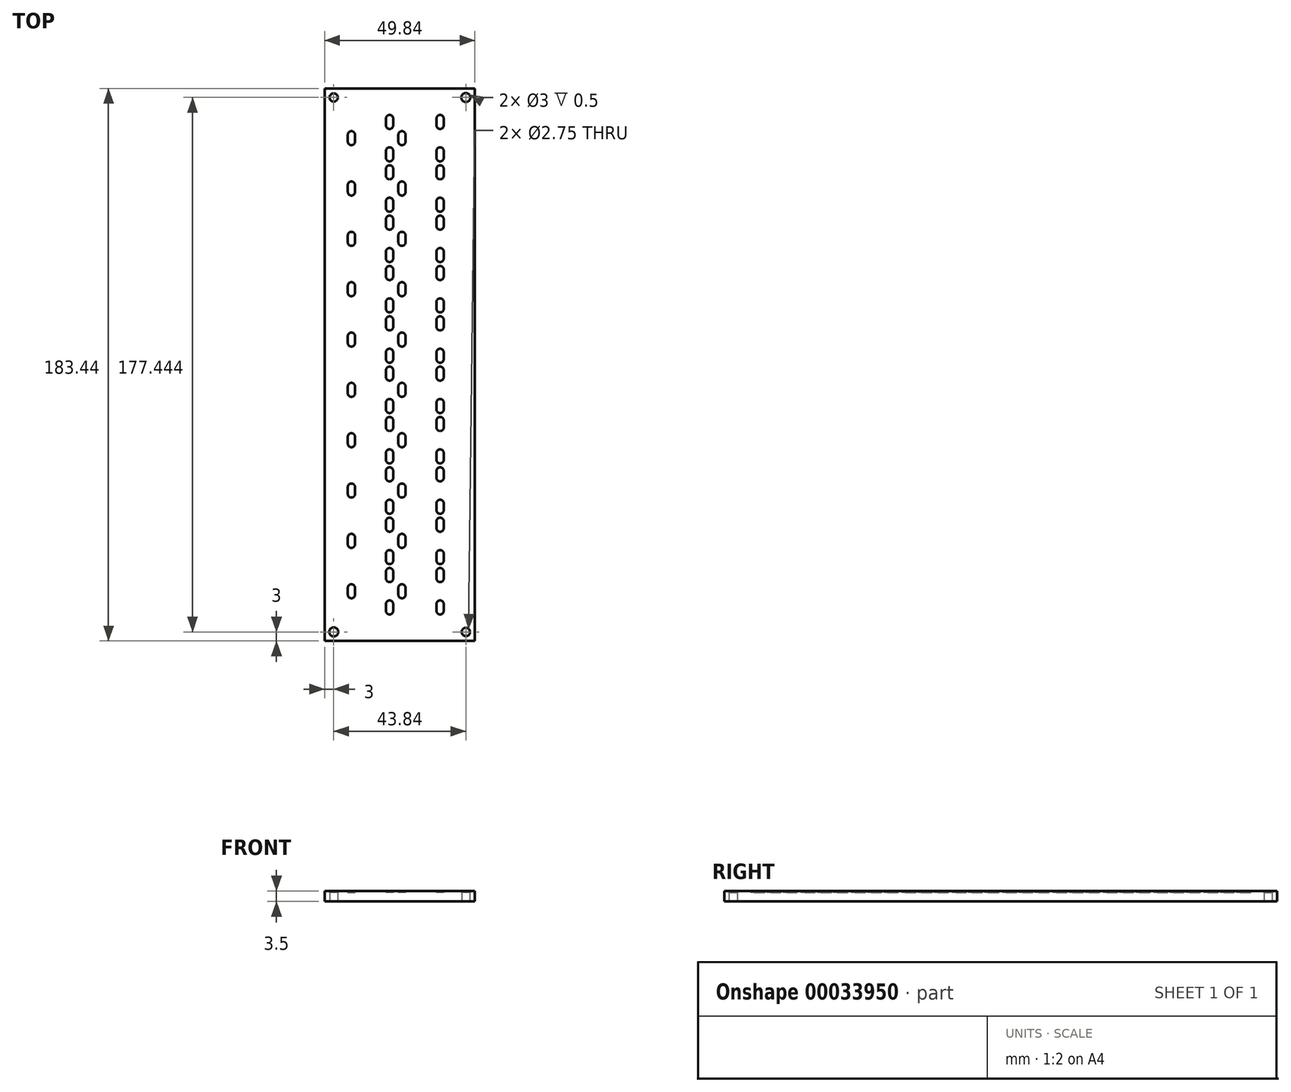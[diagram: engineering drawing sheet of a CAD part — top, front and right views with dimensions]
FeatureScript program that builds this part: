
annotation { "Feature Type Name" : "Feature", "Feature Type Description" : "" }
export const myFeature = defineFeature(function(context is Context, id is Id, definition is map)
    precondition{}
    {
        {
            var Q0;
            Q0=qCreatedBy(makeId("Top.planeOp"),FACE);
            var sketch = newSketch(context, id + "F0", { "sketchPlane" : qUnion([Q0])});
            skCircle(sketch, "E0", {"center": v(0, 0) * mm, "radius": 1.5 * mm});
            skCircle(sketch, "E1", {"center": v(43.84, 177.44) * mm, "radius": 1.5 * mm});
            skLineSegment(sketch, "E2.bottom", {"start": v(-3, 180.44) * mm, "end": v(46.84, 180.44) * mm});
            skLineSegment(sketch, "E2.top", {"start": v(-3, -3) * mm, "end": v(46.84, -3) * mm});
            skLineSegment(sketch, "E2.left", {"start": v(-3, 180.44) * mm, "end": v(-3, -3) * mm});
            skLineSegment(sketch, "E2.right", {"start": v(46.84, 180.44) * mm, "end": v(46.84, -3) * mm});
            skLineSegment(sketch, "E3.rect.left", {"start": v(19.73, 6.99) * mm, "end": v(19.73, 9.29) * mm});
            skLineSegment(sketch, "E3.rect.right", {"start": v(17.35, 6.99) * mm, "end": v(17.35, 9.29) * mm});
            skPoint(sketch, "E3.rect.middle", {"position": v(18.54, 8.14) * mm});
            skLineSegment(sketch, "E4.rect.right", {"start": v(4.68, 12.36) * mm, "end": v(4.68, 14.66) * mm});
            skLineSegment(sketch, "E4.rect.left", {"start": v(7.07, 12.36) * mm, "end": v(7.07, 14.66) * mm});
            skPoint(sketch, "E4.rect.middle", {"position": v(5.88, 13.51) * mm});
            skPoint(sketch, "E5.rect.middle", {"position": v(18.54, 18.89) * mm});
            skLineSegment(sketch, "E5.rect.left", {"start": v(19.73, 17.74) * mm, "end": v(19.73, 20.04) * mm});
            skLineSegment(sketch, "E5.rect.right", {"start": v(17.35, 17.74) * mm, "end": v(17.35, 20.04) * mm});
            skLineSegment(sketch, "E6.rect.left", {"start": v(19.73, 34.45) * mm, "end": v(19.73, 36.75) * mm});
            skPoint(sketch, "E7.rect.middle", {"position": v(18.54, 24.85) * mm});
            skPoint(sketch, "E6.rect.middle", {"position": v(18.54, 35.6) * mm});
            skLineSegment(sketch, "E6.rect.right", {"start": v(17.35, 34.45) * mm, "end": v(17.35, 36.75) * mm});
            skLineSegment(sketch, "E8.rect.left", {"start": v(7.07, 29.08) * mm, "end": v(7.07, 31.38) * mm});
            skPoint(sketch, "E8.rect.middle", {"position": v(5.88, 30.23) * mm});
            skLineSegment(sketch, "E8.rect.right", {"start": v(4.68, 29.08) * mm, "end": v(4.68, 31.38) * mm});
            skLineSegment(sketch, "E7.rect.right", {"start": v(17.35, 23.7) * mm, "end": v(17.35, 26) * mm});
            skLineSegment(sketch, "E7.rect.left", {"start": v(19.73, 23.7) * mm, "end": v(19.73, 26) * mm});
            skPoint(sketch, "E9.rect.middle", {"position": v(35.3, 8.14) * mm});
            skPoint(sketch, "E10.rect.middle", {"position": v(35.3, 35.6) * mm});
            skPoint(sketch, "E11.rect.middle", {"position": v(35.3, 24.85) * mm});
            skPoint(sketch, "E12.rect.middle", {"position": v(35.3, 18.89) * mm});
            skPoint(sketch, "E13.rect.middle", {"position": v(22.64, 13.51) * mm});
            skPoint(sketch, "E14.rect.middle", {"position": v(22.64, 30.23) * mm});
            skLineSegment(sketch, "E9.rect.left", {"start": v(36.5, 6.99) * mm, "end": v(36.5, 9.29) * mm});
            skLineSegment(sketch, "E9.rect.right", {"start": v(34.12, 6.99) * mm, "end": v(34.12, 9.29) * mm});
            skLineSegment(sketch, "E12.rect.left", {"start": v(36.5, 17.74) * mm, "end": v(36.5, 20.04) * mm});
            skLineSegment(sketch, "E12.rect.right", {"start": v(34.12, 17.74) * mm, "end": v(34.12, 20.04) * mm});
            skLineSegment(sketch, "E10.rect.right", {"start": v(34.12, 34.45) * mm, "end": v(34.12, 36.75) * mm});
            skLineSegment(sketch, "E13.rect.right", {"start": v(21.45, 12.36) * mm, "end": v(21.45, 14.66) * mm});
            skLineSegment(sketch, "E13.rect.left", {"start": v(23.83, 12.36) * mm, "end": v(23.83, 14.66) * mm});
            skLineSegment(sketch, "E10.rect.left", {"start": v(36.5, 34.45) * mm, "end": v(36.5, 36.75) * mm});
            skLineSegment(sketch, "E11.rect.left", {"start": v(36.5, 23.7) * mm, "end": v(36.5, 26) * mm});
            skLineSegment(sketch, "E14.rect.left", {"start": v(23.83, 29.08) * mm, "end": v(23.83, 31.38) * mm});
            skLineSegment(sketch, "E11.rect.right", {"start": v(34.12, 23.7) * mm, "end": v(34.12, 26) * mm});
            skLineSegment(sketch, "E14.rect.right", {"start": v(21.45, 29.08) * mm, "end": v(21.45, 31.38) * mm});
            skCircle(sketch, "E15", {"center": v(0, 177.44) * mm, "radius": 1.38 * mm});
            skCircle(sketch, "E16", {"center": v(43.84, 0) * mm, "radius": 1.38 * mm});
            skArc(sketch, "E17", {"start": v(4.68, 12.36) * mm, "mid": v(5.88, 11.17) * mm, "end": v(7.07, 12.36) * mm});
            skArc(sketch, "E18", {"start": v(7.07, 14.66) * mm, "mid": v(5.88, 15.85) * mm, "end": v(4.68, 14.66) * mm});
            skArc(sketch, "E19", {"start": v(7.07, 31.38) * mm, "mid": v(5.88, 32.57) * mm, "end": v(4.68, 31.38) * mm});
            skArc(sketch, "E20", {"start": v(4.68, 29.08) * mm, "mid": v(5.88, 27.88) * mm, "end": v(7.07, 29.08) * mm});
            skArc(sketch, "E21", {"start": v(19.73, 36.75) * mm, "mid": v(18.54, 37.94) * mm, "end": v(17.35, 36.75) * mm});
            skArc(sketch, "E22", {"start": v(17.35, 34.45) * mm, "mid": v(18.54, 33.26) * mm, "end": v(19.73, 34.45) * mm});
            skArc(sketch, "E23", {"start": v(19.73, 26) * mm, "mid": v(18.54, 27.19) * mm, "end": v(17.35, 26) * mm});
            skArc(sketch, "E24", {"start": v(17.35, 23.7) * mm, "mid": v(18.54, 22.5) * mm, "end": v(19.73, 23.7) * mm});
            skArc(sketch, "E25", {"start": v(19.73, 20.04) * mm, "mid": v(18.54, 21.23) * mm, "end": v(17.35, 20.04) * mm});
            skArc(sketch, "E26", {"start": v(17.35, 17.74) * mm, "mid": v(18.54, 16.55) * mm, "end": v(19.73, 17.74) * mm});
            skArc(sketch, "E27", {"start": v(19.73, 9.29) * mm, "mid": v(18.54, 10.48) * mm, "end": v(17.35, 9.29) * mm});
            skArc(sketch, "E28", {"start": v(17.35, 6.99) * mm, "mid": v(18.54, 5.8) * mm, "end": v(19.73, 6.99) * mm});
            skArc(sketch, "E29", {"start": v(23.83, 31.38) * mm, "mid": v(22.64, 32.57) * mm, "end": v(21.45, 31.38) * mm});
            skArc(sketch, "E30", {"start": v(21.45, 29.08) * mm, "mid": v(22.64, 27.88) * mm, "end": v(23.83, 29.08) * mm});
            skArc(sketch, "E31", {"start": v(23.83, 14.66) * mm, "mid": v(22.64, 15.85) * mm, "end": v(21.45, 14.66) * mm});
            skArc(sketch, "E32", {"start": v(21.45, 12.36) * mm, "mid": v(22.64, 11.17) * mm, "end": v(23.83, 12.36) * mm});
            skArc(sketch, "E33", {"start": v(36.5, 9.29) * mm, "mid": v(35.3, 10.48) * mm, "end": v(34.12, 9.29) * mm});
            skArc(sketch, "E34", {"start": v(34.12, 6.99) * mm, "mid": v(35.3, 5.8) * mm, "end": v(36.5, 6.99) * mm});
            skArc(sketch, "E35", {"start": v(36.5, 20.04) * mm, "mid": v(35.3, 21.23) * mm, "end": v(34.12, 20.04) * mm});
            skArc(sketch, "E36", {"start": v(34.12, 17.74) * mm, "mid": v(35.3, 16.55) * mm, "end": v(36.5, 17.74) * mm});
            skArc(sketch, "E37", {"start": v(34.12, 23.7) * mm, "mid": v(35.3, 22.5) * mm, "end": v(36.5, 23.7) * mm});
            skArc(sketch, "E38", {"start": v(36.5, 26) * mm, "mid": v(35.3, 27.19) * mm, "end": v(34.12, 26) * mm});
            skArc(sketch, "E39", {"start": v(34.12, 34.45) * mm, "mid": v(35.3, 33.26) * mm, "end": v(36.5, 34.45) * mm});
            skArc(sketch, "E40", {"start": v(36.5, 36.75) * mm, "mid": v(35.3, 37.94) * mm, "end": v(34.12, 36.75) * mm});
            skArc(sketch, "E41", {"start": v(19.73, 59.43) * mm, "mid": v(18.54, 60.62) * mm, "end": v(17.35, 59.43) * mm});
            skArc(sketch, "E42", {"start": v(23.83, 64.8) * mm, "mid": v(22.64, 66) * mm, "end": v(21.45, 64.8) * mm});
            skArc(sketch, "E43", {"start": v(4.68, 45.79) * mm, "mid": v(5.88, 44.6) * mm, "end": v(7.07, 45.79) * mm});
            skArc(sketch, "E44", {"start": v(7.07, 64.8) * mm, "mid": v(5.88, 66) * mm, "end": v(4.68, 64.8) * mm});
            skArc(sketch, "E45", {"start": v(36.5, 42.71) * mm, "mid": v(35.3, 43.9) * mm, "end": v(34.12, 42.71) * mm});
            skArc(sketch, "E46", {"start": v(23.83, 48.09) * mm, "mid": v(22.64, 49.28) * mm, "end": v(21.45, 48.09) * mm});
            skArc(sketch, "E47", {"start": v(36.5, 59.43) * mm, "mid": v(35.3, 60.62) * mm, "end": v(34.12, 59.43) * mm});
            skArc(sketch, "E48", {"start": v(19.73, 53.47) * mm, "mid": v(18.54, 54.66) * mm, "end": v(17.35, 53.47) * mm});
            skArc(sketch, "E49", {"start": v(17.35, 40.41) * mm, "mid": v(18.54, 39.22) * mm, "end": v(19.73, 40.41) * mm});
            skPoint(sketch, "E50.rect.middle", {"position": v(35.3, 58.28) * mm});
            skArc(sketch, "E51", {"start": v(36.5, 53.47) * mm, "mid": v(35.3, 54.66) * mm, "end": v(34.12, 53.47) * mm});
            skPoint(sketch, "E52.rect.middle", {"position": v(18.54, 41.56) * mm});
            skPoint(sketch, "E53.rect.middle", {"position": v(22.64, 46.94) * mm});
            skArc(sketch, "E54", {"start": v(19.73, 70.18) * mm, "mid": v(18.54, 71.37) * mm, "end": v(17.35, 70.18) * mm});
            skLineSegment(sketch, "E55.rect.right", {"start": v(17.35, 67.88) * mm, "end": v(17.35, 70.18) * mm});
            skLineSegment(sketch, "E56.rect.right", {"start": v(4.68, 62.5) * mm, "end": v(4.68, 64.8) * mm});
            skLineSegment(sketch, "E56.rect.left", {"start": v(7.07, 62.5) * mm, "end": v(7.07, 64.8) * mm});
            skLineSegment(sketch, "E53.rect.right", {"start": v(21.45, 45.79) * mm, "end": v(21.45, 48.09) * mm});
            skLineSegment(sketch, "E57.rect.left", {"start": v(19.73, 51.17) * mm, "end": v(19.73, 53.47) * mm});
            skPoint(sketch, "E55.rect.middle", {"position": v(18.54, 69.03) * mm});
            skLineSegment(sketch, "E52.rect.right", {"start": v(17.35, 40.41) * mm, "end": v(17.35, 42.71) * mm});
            skArc(sketch, "E58", {"start": v(19.73, 42.71) * mm, "mid": v(18.54, 43.9) * mm, "end": v(17.35, 42.71) * mm});
            skArc(sketch, "E59", {"start": v(17.35, 67.88) * mm, "mid": v(18.54, 66.69) * mm, "end": v(19.73, 67.88) * mm});
            skPoint(sketch, "E56.rect.middle", {"position": v(5.88, 63.65) * mm});
            skArc(sketch, "E60", {"start": v(21.45, 62.5) * mm, "mid": v(22.64, 61.31) * mm, "end": v(23.83, 62.5) * mm});
            skArc(sketch, "E61", {"start": v(17.35, 51.17) * mm, "mid": v(18.54, 49.98) * mm, "end": v(19.73, 51.17) * mm});
            skPoint(sketch, "E62.rect.middle", {"position": v(35.3, 41.56) * mm});
            skPoint(sketch, "E63.rect.middle", {"position": v(5.88, 46.94) * mm});
            skArc(sketch, "E64", {"start": v(4.68, 62.5) * mm, "mid": v(5.88, 61.31) * mm, "end": v(7.07, 62.5) * mm});
            skPoint(sketch, "E57.rect.middle", {"position": v(18.54, 52.32) * mm});
            skPoint(sketch, "E65.rect.middle", {"position": v(35.3, 69.03) * mm});
            skLineSegment(sketch, "E55.rect.left", {"start": v(19.73, 67.88) * mm, "end": v(19.73, 70.18) * mm});
            skArc(sketch, "E66", {"start": v(7.07, 48.09) * mm, "mid": v(5.88, 49.28) * mm, "end": v(4.68, 48.09) * mm});
            skLineSegment(sketch, "E57.rect.right", {"start": v(17.35, 51.17) * mm, "end": v(17.35, 53.47) * mm});
            skPoint(sketch, "E67.rect.middle", {"position": v(22.64, 63.65) * mm});
            skLineSegment(sketch, "E68.rect.left", {"start": v(19.73, 57.13) * mm, "end": v(19.73, 59.43) * mm});
            skArc(sketch, "E69", {"start": v(34.12, 40.41) * mm, "mid": v(35.3, 39.22) * mm, "end": v(36.5, 40.41) * mm});
            skLineSegment(sketch, "E68.rect.right", {"start": v(17.35, 57.13) * mm, "end": v(17.35, 59.43) * mm});
            skArc(sketch, "E70", {"start": v(34.12, 57.13) * mm, "mid": v(35.3, 55.93) * mm, "end": v(36.5, 57.13) * mm});
            skLineSegment(sketch, "E52.rect.left", {"start": v(19.73, 40.41) * mm, "end": v(19.73, 42.71) * mm});
            skLineSegment(sketch, "E65.rect.left", {"start": v(36.5, 67.88) * mm, "end": v(36.5, 70.18) * mm});
            skPoint(sketch, "E71.rect.middle", {"position": v(35.3, 52.32) * mm});
            skLineSegment(sketch, "E53.rect.left", {"start": v(23.83, 45.79) * mm, "end": v(23.83, 48.09) * mm});
            skLineSegment(sketch, "E50.rect.left", {"start": v(36.5, 57.13) * mm, "end": v(36.5, 59.43) * mm});
            skLineSegment(sketch, "E63.rect.right", {"start": v(4.68, 45.79) * mm, "end": v(4.68, 48.09) * mm});
            skLineSegment(sketch, "E71.rect.left", {"start": v(36.5, 51.17) * mm, "end": v(36.5, 53.47) * mm});
            skArc(sketch, "E72", {"start": v(17.35, 57.13) * mm, "mid": v(18.54, 55.93) * mm, "end": v(19.73, 57.13) * mm});
            skLineSegment(sketch, "E63.rect.left", {"start": v(7.07, 45.79) * mm, "end": v(7.07, 48.09) * mm});
            skLineSegment(sketch, "E67.rect.left", {"start": v(23.83, 62.5) * mm, "end": v(23.83, 64.8) * mm});
            skLineSegment(sketch, "E50.rect.right", {"start": v(34.12, 57.13) * mm, "end": v(34.12, 59.43) * mm});
            skLineSegment(sketch, "E71.rect.right", {"start": v(34.12, 51.17) * mm, "end": v(34.12, 53.47) * mm});
            skLineSegment(sketch, "E62.rect.left", {"start": v(36.5, 40.41) * mm, "end": v(36.5, 42.71) * mm});
            skLineSegment(sketch, "E62.rect.right", {"start": v(34.12, 40.41) * mm, "end": v(34.12, 42.71) * mm});
            skArc(sketch, "E73", {"start": v(34.12, 51.17) * mm, "mid": v(35.3, 49.98) * mm, "end": v(36.5, 51.17) * mm});
            skPoint(sketch, "E68.rect.middle", {"position": v(18.54, 58.28) * mm});
            skLineSegment(sketch, "E67.rect.right", {"start": v(21.45, 62.5) * mm, "end": v(21.45, 64.8) * mm});
            skArc(sketch, "E74", {"start": v(34.12, 67.88) * mm, "mid": v(35.3, 66.69) * mm, "end": v(36.5, 67.88) * mm});
            skLineSegment(sketch, "E65.rect.right", {"start": v(34.12, 67.88) * mm, "end": v(34.12, 70.18) * mm});
            skArc(sketch, "E75", {"start": v(21.45, 45.79) * mm, "mid": v(22.64, 44.6) * mm, "end": v(23.83, 45.79) * mm});
            skArc(sketch, "E76", {"start": v(36.5, 70.18) * mm, "mid": v(35.3, 71.37) * mm, "end": v(34.12, 70.18) * mm});
            skArc(sketch, "E77", {"start": v(36.5, 109.57) * mm, "mid": v(35.3, 110.76) * mm, "end": v(34.12, 109.57) * mm});
            skArc(sketch, "E78", {"start": v(7.07, 98.23) * mm, "mid": v(5.88, 99.42) * mm, "end": v(4.68, 98.23) * mm});
            skPoint(sketch, "E79.rect.middle", {"position": v(18.54, 74.99) * mm});
            skArc(sketch, "E80", {"start": v(4.68, 112.64) * mm, "mid": v(5.88, 111.45) * mm, "end": v(7.07, 112.64) * mm});
            skArc(sketch, "E81", {"start": v(36.5, 126.28) * mm, "mid": v(35.3, 127.47) * mm, "end": v(34.12, 126.28) * mm});
            skPoint(sketch, "E82.rect.middle", {"position": v(18.54, 108.42) * mm});
            skArc(sketch, "E83", {"start": v(36.5, 92.85) * mm, "mid": v(35.3, 94.04) * mm, "end": v(34.12, 92.85) * mm});
            skArc(sketch, "E84", {"start": v(7.07, 131.66) * mm, "mid": v(5.88, 132.85) * mm, "end": v(4.68, 131.66) * mm});
            skArc(sketch, "E85", {"start": v(36.5, 76.14) * mm, "mid": v(35.3, 77.33) * mm, "end": v(34.12, 76.14) * mm});
            skArc(sketch, "E86", {"start": v(4.68, 79.22) * mm, "mid": v(5.88, 78.02) * mm, "end": v(7.07, 79.22) * mm});
            skArc(sketch, "E87", {"start": v(17.35, 73.84) * mm, "mid": v(18.54, 72.65) * mm, "end": v(19.73, 73.84) * mm});
            skArc(sketch, "E88", {"start": v(21.45, 95.93) * mm, "mid": v(22.64, 94.74) * mm, "end": v(23.83, 95.93) * mm});
            skPoint(sketch, "E89.rect.middle", {"position": v(35.3, 119.17) * mm});
            skPoint(sketch, "E90.rect.middle", {"position": v(35.3, 102.46) * mm});
            skArc(sketch, "E91", {"start": v(34.12, 107.27) * mm, "mid": v(35.3, 106.07) * mm, "end": v(36.5, 107.27) * mm});
            skPoint(sketch, "E92.rect.middle", {"position": v(5.88, 130.5) * mm});
            skArc(sketch, "E93", {"start": v(19.73, 92.85) * mm, "mid": v(18.54, 94.04) * mm, "end": v(17.35, 92.85) * mm});
            skPoint(sketch, "E94.rect.middle", {"position": v(35.3, 108.42) * mm});
            skArc(sketch, "E95", {"start": v(17.35, 107.27) * mm, "mid": v(18.54, 106.07) * mm, "end": v(19.73, 107.27) * mm});
            skArc(sketch, "E96", {"start": v(17.35, 84.6) * mm, "mid": v(18.54, 83.4) * mm, "end": v(19.73, 84.6) * mm});
            skPoint(sketch, "E97.rect.middle", {"position": v(22.64, 130.5) * mm});
            skArc(sketch, "E98", {"start": v(34.12, 73.84) * mm, "mid": v(35.3, 72.65) * mm, "end": v(36.5, 73.84) * mm});
            skPoint(sketch, "E99.rect.middle", {"position": v(18.54, 119.17) * mm});
            skPoint(sketch, "E100.rect.middle", {"position": v(5.88, 80.37) * mm});
            skPoint(sketch, "E101.rect.middle", {"position": v(18.54, 125.13) * mm});
            skArc(sketch, "E102", {"start": v(4.68, 95.93) * mm, "mid": v(5.88, 94.74) * mm, "end": v(7.07, 95.93) * mm});
            skArc(sketch, "E103", {"start": v(23.83, 131.66) * mm, "mid": v(22.64, 132.85) * mm, "end": v(21.45, 131.66) * mm});
            skArc(sketch, "E104", {"start": v(23.83, 98.23) * mm, "mid": v(22.64, 99.42) * mm, "end": v(21.45, 98.23) * mm});
            skPoint(sketch, "E105.rect.middle", {"position": v(5.88, 97.08) * mm});
            skArc(sketch, "E106", {"start": v(19.73, 76.14) * mm, "mid": v(18.54, 77.33) * mm, "end": v(17.35, 76.14) * mm});
            skPoint(sketch, "E107.rect.middle", {"position": v(35.3, 125.13) * mm});
            skArc(sketch, "E108", {"start": v(23.83, 81.52) * mm, "mid": v(22.64, 82.7) * mm, "end": v(21.45, 81.52) * mm});
            skPoint(sketch, "E109.rect.middle", {"position": v(18.54, 85.74) * mm});
            skPoint(sketch, "E110.rect.middle", {"position": v(22.64, 113.8) * mm});
            skPoint(sketch, "E111.rect.middle", {"position": v(22.64, 97.08) * mm});
            skPoint(sketch, "E112.rect.middle", {"position": v(35.3, 91.7) * mm});
            skArc(sketch, "E113", {"start": v(23.83, 114.94) * mm, "mid": v(22.64, 116.13) * mm, "end": v(21.45, 114.94) * mm});
            skArc(sketch, "E114", {"start": v(7.07, 81.52) * mm, "mid": v(5.88, 82.7) * mm, "end": v(4.68, 81.52) * mm});
            skArc(sketch, "E115", {"start": v(19.73, 126.28) * mm, "mid": v(18.54, 127.47) * mm, "end": v(17.35, 126.28) * mm});
            skPoint(sketch, "E116.rect.middle", {"position": v(35.3, 135.88) * mm});
            skArc(sketch, "E117", {"start": v(7.07, 114.94) * mm, "mid": v(5.88, 116.13) * mm, "end": v(4.68, 114.94) * mm});
            skArc(sketch, "E118", {"start": v(21.45, 79.22) * mm, "mid": v(22.64, 78.02) * mm, "end": v(23.83, 79.22) * mm});
            skPoint(sketch, "E119.rect.middle", {"position": v(5.88, 113.8) * mm});
            skArc(sketch, "E120", {"start": v(21.45, 112.64) * mm, "mid": v(22.64, 111.45) * mm, "end": v(23.83, 112.64) * mm});
            skPoint(sketch, "E121.rect.middle", {"position": v(35.3, 85.74) * mm});
            skArc(sketch, "E122", {"start": v(34.12, 84.6) * mm, "mid": v(35.3, 83.4) * mm, "end": v(36.5, 84.6) * mm});
            skPoint(sketch, "E123.rect.middle", {"position": v(18.54, 135.88) * mm});
            skArc(sketch, "E124", {"start": v(17.35, 123.98) * mm, "mid": v(18.54, 122.79) * mm, "end": v(19.73, 123.98) * mm});
            skPoint(sketch, "E125.rect.middle", {"position": v(18.54, 102.46) * mm});
            skPoint(sketch, "E126.rect.middle", {"position": v(35.3, 74.99) * mm});
            skPoint(sketch, "E127.rect.middle", {"position": v(18.54, 91.7) * mm});
            skPoint(sketch, "E128.rect.middle", {"position": v(22.64, 80.37) * mm});
            skLineSegment(sketch, "E99.rect.right", {"start": v(17.35, 118.02) * mm, "end": v(17.35, 120.32) * mm});
            skArc(sketch, "E129", {"start": v(36.5, 86.9) * mm, "mid": v(35.3, 88.08) * mm, "end": v(34.12, 86.9) * mm});
            skLineSegment(sketch, "E94.rect.right", {"start": v(34.12, 107.27) * mm, "end": v(34.12, 109.57) * mm});
            skLineSegment(sketch, "E126.rect.left", {"start": v(36.5, 73.84) * mm, "end": v(36.5, 76.14) * mm});
            skArc(sketch, "E130", {"start": v(19.73, 86.9) * mm, "mid": v(18.54, 88.08) * mm, "end": v(17.35, 86.9) * mm});
            skLineSegment(sketch, "E125.rect.left", {"start": v(19.73, 101.3) * mm, "end": v(19.73, 103.6) * mm});
            skLineSegment(sketch, "E128.rect.left", {"start": v(23.83, 79.22) * mm, "end": v(23.83, 81.52) * mm});
            skArc(sketch, "E131", {"start": v(34.12, 90.55) * mm, "mid": v(35.3, 89.36) * mm, "end": v(36.5, 90.55) * mm});
            skArc(sketch, "E132", {"start": v(19.73, 103.6) * mm, "mid": v(18.54, 104.8) * mm, "end": v(17.35, 103.6) * mm});
            skArc(sketch, "E133", {"start": v(19.73, 109.57) * mm, "mid": v(18.54, 110.76) * mm, "end": v(17.35, 109.57) * mm});
            skLineSegment(sketch, "E116.rect.right", {"start": v(34.12, 134.73) * mm, "end": v(34.12, 137.03) * mm});
            skArc(sketch, "E134", {"start": v(17.35, 90.55) * mm, "mid": v(18.54, 89.36) * mm, "end": v(19.73, 90.55) * mm});
            skLineSegment(sketch, "E99.rect.left", {"start": v(19.73, 118.02) * mm, "end": v(19.73, 120.32) * mm});
            skArc(sketch, "E135", {"start": v(19.73, 120.32) * mm, "mid": v(18.54, 121.5) * mm, "end": v(17.35, 120.32) * mm});
            skLineSegment(sketch, "E125.rect.right", {"start": v(17.35, 101.3) * mm, "end": v(17.35, 103.6) * mm});
            skLineSegment(sketch, "E116.rect.left", {"start": v(36.5, 134.73) * mm, "end": v(36.5, 137.03) * mm});
            skLineSegment(sketch, "E126.rect.right", {"start": v(34.12, 73.84) * mm, "end": v(34.12, 76.14) * mm});
            skLineSegment(sketch, "E110.rect.left", {"start": v(23.83, 112.64) * mm, "end": v(23.83, 114.94) * mm});
            skArc(sketch, "E136", {"start": v(36.5, 137.03) * mm, "mid": v(35.3, 138.22) * mm, "end": v(34.12, 137.03) * mm});
            skArc(sketch, "E137", {"start": v(34.12, 123.98) * mm, "mid": v(35.3, 122.79) * mm, "end": v(36.5, 123.98) * mm});
            skArc(sketch, "E138", {"start": v(21.45, 129.36) * mm, "mid": v(22.64, 128.16) * mm, "end": v(23.83, 129.36) * mm});
            skArc(sketch, "E139", {"start": v(4.68, 129.36) * mm, "mid": v(5.88, 128.16) * mm, "end": v(7.07, 129.36) * mm});
            skArc(sketch, "E140", {"start": v(19.73, 137.03) * mm, "mid": v(18.54, 138.22) * mm, "end": v(17.35, 137.03) * mm});
            skLineSegment(sketch, "E111.rect.right", {"start": v(21.45, 95.93) * mm, "end": v(21.45, 98.23) * mm});
            skArc(sketch, "E141", {"start": v(34.12, 118.02) * mm, "mid": v(35.3, 116.83) * mm, "end": v(36.5, 118.02) * mm});
            skLineSegment(sketch, "E109.rect.left", {"start": v(19.73, 84.6) * mm, "end": v(19.73, 86.9) * mm});
            skLineSegment(sketch, "E127.rect.left", {"start": v(19.73, 90.55) * mm, "end": v(19.73, 92.85) * mm});
            skLineSegment(sketch, "E127.rect.right", {"start": v(17.35, 90.55) * mm, "end": v(17.35, 92.85) * mm});
            skLineSegment(sketch, "E79.rect.right", {"start": v(17.35, 73.84) * mm, "end": v(17.35, 76.14) * mm});
            skLineSegment(sketch, "E107.rect.left", {"start": v(36.5, 123.98) * mm, "end": v(36.5, 126.28) * mm});
            skLineSegment(sketch, "E82.rect.left", {"start": v(19.73, 107.27) * mm, "end": v(19.73, 109.57) * mm});
            skLineSegment(sketch, "E123.rect.right", {"start": v(17.35, 134.73) * mm, "end": v(17.35, 137.03) * mm});
            skLineSegment(sketch, "E82.rect.right", {"start": v(17.35, 107.27) * mm, "end": v(17.35, 109.57) * mm});
            skArc(sketch, "E142", {"start": v(36.5, 103.6) * mm, "mid": v(35.3, 104.8) * mm, "end": v(34.12, 103.6) * mm});
            skLineSegment(sketch, "E97.rect.right", {"start": v(21.45, 129.36) * mm, "end": v(21.45, 131.66) * mm});
            skLineSegment(sketch, "E112.rect.right", {"start": v(34.12, 90.55) * mm, "end": v(34.12, 92.85) * mm});
            skLineSegment(sketch, "E119.rect.left", {"start": v(7.07, 112.64) * mm, "end": v(7.07, 114.94) * mm});
            skArc(sketch, "E143", {"start": v(17.35, 101.3) * mm, "mid": v(18.54, 100.11) * mm, "end": v(19.73, 101.3) * mm});
            skArc(sketch, "E144", {"start": v(17.35, 118.02) * mm, "mid": v(18.54, 116.83) * mm, "end": v(19.73, 118.02) * mm});
            skLineSegment(sketch, "E123.rect.left", {"start": v(19.73, 134.73) * mm, "end": v(19.73, 137.03) * mm});
            skArc(sketch, "E145", {"start": v(17.35, 134.73) * mm, "mid": v(18.54, 133.54) * mm, "end": v(19.73, 134.73) * mm});
            skLineSegment(sketch, "E97.rect.left", {"start": v(23.83, 129.36) * mm, "end": v(23.83, 131.66) * mm});
            skLineSegment(sketch, "E90.rect.left", {"start": v(36.5, 101.3) * mm, "end": v(36.5, 103.6) * mm});
            skLineSegment(sketch, "E121.rect.right", {"start": v(34.12, 84.6) * mm, "end": v(34.12, 86.9) * mm});
            skLineSegment(sketch, "E107.rect.right", {"start": v(34.12, 123.98) * mm, "end": v(34.12, 126.28) * mm});
            skLineSegment(sketch, "E112.rect.left", {"start": v(36.5, 90.55) * mm, "end": v(36.5, 92.85) * mm});
            skLineSegment(sketch, "E94.rect.left", {"start": v(36.5, 107.27) * mm, "end": v(36.5, 109.57) * mm});
            skLineSegment(sketch, "E92.rect.left", {"start": v(7.07, 129.36) * mm, "end": v(7.07, 131.66) * mm});
            skLineSegment(sketch, "E90.rect.right", {"start": v(34.12, 101.3) * mm, "end": v(34.12, 103.6) * mm});
            skLineSegment(sketch, "E101.rect.left", {"start": v(19.73, 123.98) * mm, "end": v(19.73, 126.28) * mm});
            skLineSegment(sketch, "E109.rect.right", {"start": v(17.35, 84.6) * mm, "end": v(17.35, 86.9) * mm});
            skLineSegment(sketch, "E119.rect.right", {"start": v(4.68, 112.64) * mm, "end": v(4.68, 114.94) * mm});
            skArc(sketch, "E146", {"start": v(36.5, 120.32) * mm, "mid": v(35.3, 121.5) * mm, "end": v(34.12, 120.32) * mm});
            skArc(sketch, "E147", {"start": v(34.12, 134.73) * mm, "mid": v(35.3, 133.54) * mm, "end": v(36.5, 134.73) * mm});
            skLineSegment(sketch, "E92.rect.right", {"start": v(4.68, 129.36) * mm, "end": v(4.68, 131.66) * mm});
            skLineSegment(sketch, "E79.rect.left", {"start": v(19.73, 73.84) * mm, "end": v(19.73, 76.14) * mm});
            skLineSegment(sketch, "E89.rect.left", {"start": v(36.5, 118.02) * mm, "end": v(36.5, 120.32) * mm});
            skLineSegment(sketch, "E89.rect.right", {"start": v(34.12, 118.02) * mm, "end": v(34.12, 120.32) * mm});
            skLineSegment(sketch, "E110.rect.right", {"start": v(21.45, 112.64) * mm, "end": v(21.45, 114.94) * mm});
            skArc(sketch, "E148", {"start": v(34.12, 101.3) * mm, "mid": v(35.3, 100.11) * mm, "end": v(36.5, 101.3) * mm});
            skLineSegment(sketch, "E105.rect.left", {"start": v(7.07, 95.93) * mm, "end": v(7.07, 98.23) * mm});
            skLineSegment(sketch, "E105.rect.right", {"start": v(4.68, 95.93) * mm, "end": v(4.68, 98.23) * mm});
            skLineSegment(sketch, "E101.rect.right", {"start": v(17.35, 123.98) * mm, "end": v(17.35, 126.28) * mm});
            skLineSegment(sketch, "E128.rect.right", {"start": v(21.45, 79.22) * mm, "end": v(21.45, 81.52) * mm});
            skLineSegment(sketch, "E111.rect.left", {"start": v(23.83, 95.93) * mm, "end": v(23.83, 98.23) * mm});
            skLineSegment(sketch, "E121.rect.left", {"start": v(36.5, 84.6) * mm, "end": v(36.5, 86.9) * mm});
            skLineSegment(sketch, "E100.rect.right", {"start": v(4.68, 79.22) * mm, "end": v(4.68, 81.52) * mm});
            skLineSegment(sketch, "E100.rect.left", {"start": v(7.07, 79.22) * mm, "end": v(7.07, 81.52) * mm});
            skArc(sketch, "E149", {"start": v(34.12, 168.16) * mm, "mid": v(35.3, 166.97) * mm, "end": v(36.5, 168.16) * mm});
            skPoint(sketch, "E150.rect.middle", {"position": v(18.54, 141.84) * mm});
            skPoint(sketch, "E151.rect.middle", {"position": v(35.3, 152.6) * mm});
            skArc(sketch, "E152", {"start": v(36.5, 143) * mm, "mid": v(35.3, 144.18) * mm, "end": v(34.12, 143) * mm});
            skArc(sketch, "E153", {"start": v(7.07, 165.08) * mm, "mid": v(5.88, 166.27) * mm, "end": v(4.68, 165.08) * mm});
            skPoint(sketch, "E154.rect.middle", {"position": v(35.3, 158.56) * mm});
            skArc(sketch, "E155", {"start": v(36.5, 170.46) * mm, "mid": v(35.3, 171.65) * mm, "end": v(34.12, 170.46) * mm});
            skArc(sketch, "E156", {"start": v(4.68, 146.07) * mm, "mid": v(5.88, 144.88) * mm, "end": v(7.07, 146.07) * mm});
            skArc(sketch, "E157", {"start": v(19.73, 170.46) * mm, "mid": v(18.54, 171.65) * mm, "end": v(17.35, 170.46) * mm});
            skPoint(sketch, "E158.rect.middle", {"position": v(35.3, 169.3) * mm});
            skArc(sketch, "E159", {"start": v(36.5, 159.7) * mm, "mid": v(35.3, 160.9) * mm, "end": v(34.12, 159.7) * mm});
            skArc(sketch, "E160", {"start": v(34.12, 151.45) * mm, "mid": v(35.3, 150.25) * mm, "end": v(36.5, 151.45) * mm});
            skPoint(sketch, "E161.rect.middle", {"position": v(22.64, 147.22) * mm});
            skArc(sketch, "E162", {"start": v(21.45, 146.07) * mm, "mid": v(22.64, 144.88) * mm, "end": v(23.83, 146.07) * mm});
            skArc(sketch, "E163", {"start": v(17.35, 157.4) * mm, "mid": v(18.54, 156.21) * mm, "end": v(19.73, 157.4) * mm});
            skArc(sketch, "E164", {"start": v(19.73, 153.75) * mm, "mid": v(18.54, 154.94) * mm, "end": v(17.35, 153.75) * mm});
            skPoint(sketch, "E165.rect.middle", {"position": v(5.88, 163.93) * mm});
            skArc(sketch, "E166", {"start": v(4.68, 162.78) * mm, "mid": v(5.88, 161.6) * mm, "end": v(7.07, 162.78) * mm});
            skPoint(sketch, "E167.rect.middle", {"position": v(35.3, 141.84) * mm});
            skArc(sketch, "E168", {"start": v(34.12, 157.4) * mm, "mid": v(35.3, 156.21) * mm, "end": v(36.5, 157.4) * mm});
            skPoint(sketch, "E169.rect.middle", {"position": v(5.88, 147.22) * mm});
            skArc(sketch, "E170", {"start": v(19.73, 143) * mm, "mid": v(18.54, 144.18) * mm, "end": v(17.35, 143) * mm});
            skArc(sketch, "E171", {"start": v(7.07, 148.37) * mm, "mid": v(5.88, 149.56) * mm, "end": v(4.68, 148.37) * mm});
            skPoint(sketch, "E172.rect.middle", {"position": v(18.54, 169.3) * mm});
            skArc(sketch, "E173", {"start": v(21.45, 162.78) * mm, "mid": v(22.64, 161.6) * mm, "end": v(23.83, 162.78) * mm});
            skArc(sketch, "E174", {"start": v(36.5, 153.75) * mm, "mid": v(35.3, 154.94) * mm, "end": v(34.12, 153.75) * mm});
            skPoint(sketch, "E175.rect.middle", {"position": v(22.64, 163.93) * mm});
            skArc(sketch, "E176", {"start": v(23.83, 165.08) * mm, "mid": v(22.64, 166.27) * mm, "end": v(21.45, 165.08) * mm});
            skPoint(sketch, "E177.rect.middle", {"position": v(18.54, 152.6) * mm});
            skArc(sketch, "E178", {"start": v(17.35, 151.45) * mm, "mid": v(18.54, 150.25) * mm, "end": v(19.73, 151.45) * mm});
            skArc(sketch, "E179", {"start": v(19.73, 159.7) * mm, "mid": v(18.54, 160.9) * mm, "end": v(17.35, 159.7) * mm});
            skArc(sketch, "E180", {"start": v(23.83, 148.37) * mm, "mid": v(22.64, 149.56) * mm, "end": v(21.45, 148.37) * mm});
            skPoint(sketch, "E181.rect.middle", {"position": v(18.54, 158.56) * mm});
            skArc(sketch, "E182", {"start": v(17.35, 168.16) * mm, "mid": v(18.54, 166.97) * mm, "end": v(19.73, 168.16) * mm});
            skLineSegment(sketch, "E154.rect.left", {"start": v(36.5, 157.4) * mm, "end": v(36.5, 159.7) * mm});
            skLineSegment(sketch, "E161.rect.left", {"start": v(23.83, 146.07) * mm, "end": v(23.83, 148.37) * mm});
            skLineSegment(sketch, "E158.rect.left", {"start": v(36.5, 168.16) * mm, "end": v(36.5, 170.46) * mm});
            skArc(sketch, "E183", {"start": v(34.12, 140.7) * mm, "mid": v(35.3, 139.5) * mm, "end": v(36.5, 140.7) * mm});
            skLineSegment(sketch, "E177.rect.left", {"start": v(19.73, 151.45) * mm, "end": v(19.73, 153.75) * mm});
            skLineSegment(sketch, "E151.rect.right", {"start": v(34.12, 151.45) * mm, "end": v(34.12, 153.75) * mm});
            skLineSegment(sketch, "E150.rect.left", {"start": v(19.73, 140.7) * mm, "end": v(19.73, 143) * mm});
            skLineSegment(sketch, "E167.rect.left", {"start": v(36.5, 140.7) * mm, "end": v(36.5, 143) * mm});
            skLineSegment(sketch, "E161.rect.right", {"start": v(21.45, 146.07) * mm, "end": v(21.45, 148.37) * mm});
            skLineSegment(sketch, "E150.rect.right", {"start": v(17.35, 140.7) * mm, "end": v(17.35, 143) * mm});
            skLineSegment(sketch, "E167.rect.right", {"start": v(34.12, 140.7) * mm, "end": v(34.12, 143) * mm});
            skArc(sketch, "E184", {"start": v(17.35, 140.7) * mm, "mid": v(18.54, 139.5) * mm, "end": v(19.73, 140.7) * mm});
            skLineSegment(sketch, "E151.rect.left", {"start": v(36.5, 151.45) * mm, "end": v(36.5, 153.75) * mm});
            skLineSegment(sketch, "E154.rect.right", {"start": v(34.12, 157.4) * mm, "end": v(34.12, 159.7) * mm});
            skLineSegment(sketch, "E165.rect.left", {"start": v(7.07, 162.78) * mm, "end": v(7.07, 165.08) * mm});
            skLineSegment(sketch, "E172.rect.right", {"start": v(17.35, 168.16) * mm, "end": v(17.35, 170.46) * mm});
            skLineSegment(sketch, "E169.rect.right", {"start": v(4.68, 146.07) * mm, "end": v(4.68, 148.37) * mm});
            skLineSegment(sketch, "E175.rect.left", {"start": v(23.83, 162.78) * mm, "end": v(23.83, 165.08) * mm});
            skLineSegment(sketch, "E169.rect.left", {"start": v(7.07, 146.07) * mm, "end": v(7.07, 148.37) * mm});
            skLineSegment(sketch, "E181.rect.right", {"start": v(17.35, 157.4) * mm, "end": v(17.35, 159.7) * mm});
            skLineSegment(sketch, "E175.rect.right", {"start": v(21.45, 162.78) * mm, "end": v(21.45, 165.08) * mm});
            skLineSegment(sketch, "E165.rect.right", {"start": v(4.68, 162.78) * mm, "end": v(4.68, 165.08) * mm});
            skLineSegment(sketch, "E177.rect.right", {"start": v(17.35, 151.45) * mm, "end": v(17.35, 153.75) * mm});
            skLineSegment(sketch, "E172.rect.left", {"start": v(19.73, 168.16) * mm, "end": v(19.73, 170.46) * mm});
            skLineSegment(sketch, "E158.rect.right", {"start": v(34.12, 168.16) * mm, "end": v(34.12, 170.46) * mm});
            skLineSegment(sketch, "E181.rect.left", {"start": v(19.73, 157.4) * mm, "end": v(19.73, 159.7) * mm});
            skSolve(sketch);
        }
        {
            var Q0;
            Q0=makeQuery(id+"F0.imprint","IMPRINT",FACE,{"disambiguationData":[TD([[makeQuery(id+"F0.imprint","IMPRINT",EDGE,{"derivedFrom":sQuery(id+"F0.wireOp",EDGE,"E0")}),-1.0]])]});
            extrude(context, id + "F1", {"entities" : qUnion([Q0]), "depth" : .5 * mm});
        }
        {
            var Q0;
            Q0=makeQuery(id+"F1.opExtrude","CAP_FACE",FACE,{"disambiguationData":[OSD([sQuery(id+"F0.wireOp",EDGE,"E0"),sQuery(id+"F0.wireOp",EDGE,"E1"),sQuery(id+"F0.wireOp",EDGE,"E2.bottom"),sQuery(id+"F0.wireOp",EDGE,"E2.top"),sQuery(id+"F0.wireOp",EDGE,"E2.left"),sQuery(id+"F0.wireOp",EDGE,"E2.right"),sQuery(id+"F0.wireOp",EDGE,"E3.rect.bottom"),sQuery(id+"F0.wireOp",EDGE,"E3.rect.top"),sQuery(id+"F0.wireOp",EDGE,"E3.rect.left"),sQuery(id+"F0.wireOp",EDGE,"E3.rect.right"),sQuery(id+"F0.wireOp",EDGE,"E4.rect.right"),sQuery(id+"F0.wireOp",EDGE,"E4.rect.left"),sQuery(id+"F0.wireOp",EDGE,"E4.rect.top"),sQuery(id+"F0.wireOp",EDGE,"E4.rect.bottom"),sQuery(id+"F0.wireOp",EDGE,"E5.rect.top"),sQuery(id+"F0.wireOp",EDGE,"E5.rect.bottom"),sQuery(id+"F0.wireOp",EDGE,"E5.rect.left"),sQuery(id+"F0.wireOp",EDGE,"E5.rect.right"),sQuery(id+"F0.wireOp",EDGE,"E7.rect.top"),sQuery(id+"F0.wireOp",EDGE,"E6.rect.left"),sQuery(id+"F0.wireOp",EDGE,"E7.rect.bottom"),sQuery(id+"F0.wireOp",EDGE,"E8.rect.top"),sQuery(id+"F0.wireOp",EDGE,"E6.rect.bottom"),sQuery(id+"F0.wireOp",EDGE,"E6.rect.top"),sQuery(id+"F0.wireOp",EDGE,"E8.rect.bottom"),sQuery(id+"F0.wireOp",EDGE,"E6.rect.right"),sQuery(id+"F0.wireOp",EDGE,"E8.rect.left"),sQuery(id+"F0.wireOp",EDGE,"E8.rect.right"),sQuery(id+"F0.wireOp",EDGE,"E7.rect.right"),sQuery(id+"F0.wireOp",EDGE,"E7.rect.left"),sQuery(id+"F0.wireOp",EDGE,"b43a0ba4-9dba-46bc-968b-13e96fca23b3.rect.left"),sQuery(id+"F0.wireOp",EDGE,"b43a0ba4-9dba-46bc-968b-13e96fca23b3.rect.bottom"),sQuery(id+"F0.wireOp",EDGE,"7761b7ab-5946-4f6e-ad21-f6075cb1ff51.rect.top"),sQuery(id+"F0.wireOp",EDGE,"4726b28d-0386-4670-8967-bc6313adf6ef.rect.right"),sQuery(id+"F0.wireOp",EDGE,"7761b7ab-5946-4f6e-ad21-f6075cb1ff51.rect.right"),sQuery(id+"F0.wireOp",EDGE,"4726b28d-0386-4670-8967-bc6313adf6ef.rect.top"),sQuery(id+"F0.wireOp",EDGE,"b43a0ba4-9dba-46bc-968b-13e96fca23b3.rect.right"),sQuery(id+"F0.wireOp",EDGE,"4726b28d-0386-4670-8967-bc6313adf6ef.rect.bottom"),sQuery(id+"F0.wireOp",EDGE,"4726b28d-0386-4670-8967-bc6313adf6ef.rect.left"),sQuery(id+"F0.wireOp",EDGE,"7761b7ab-5946-4f6e-ad21-f6075cb1ff51.rect.left"),sQuery(id+"F0.wireOp",EDGE,"b43a0ba4-9dba-46bc-968b-13e96fca23b3.rect.top"),sQuery(id+"F0.wireOp",EDGE,"7761b7ab-5946-4f6e-ad21-f6075cb1ff51.rect.bottom"),sQuery(id+"F0.wireOp",EDGE,"57ca4f26-5c56-4c68-9457-4a64392f3347.rect.left"),sQuery(id+"F0.wireOp",EDGE,"0ff1be2a-a1a8-4b6e-9f00-62856e441f21.rect.right"),sQuery(id+"F0.wireOp",EDGE,"208a584b-ce05-4589-bfe7-39b1698a8194.rect.left"),sQuery(id+"F0.wireOp",EDGE,"3fd6ee33-8733-46eb-a767-dbbe76983c7d.rect.left"),sQuery(id+"F0.wireOp",EDGE,"7a9b5616-fe8a-4a4b-9298-42c4a7e55be2.rect.right"),sQuery(id+"F0.wireOp",EDGE,"04949f4e-e150-414f-b18a-4da78bc3358c.rect.right"),sQuery(id+"F0.wireOp",EDGE,"208a584b-ce05-4589-bfe7-39b1698a8194.rect.right"),sQuery(id+"F0.wireOp",EDGE,"7a9b5616-fe8a-4a4b-9298-42c4a7e55be2.rect.left"),sQuery(id+"F0.wireOp",EDGE,"3fd6ee33-8733-46eb-a767-dbbe76983c7d.rect.right"),sQuery(id+"F0.wireOp",EDGE,"04949f4e-e150-414f-b18a-4da78bc3358c.rect.left"),sQuery(id+"F0.wireOp",EDGE,"57ca4f26-5c56-4c68-9457-4a64392f3347.rect.right"),sQuery(id+"F0.wireOp",EDGE,"0ff1be2a-a1a8-4b6e-9f00-62856e441f21.rect.left"),sQuery(id+"F0.wireOp",EDGE,"04949f4e-e150-414f-b18a-4da78bc3358c.rect.top"),sQuery(id+"F0.wireOp",EDGE,"208a584b-ce05-4589-bfe7-39b1698a8194.rect.bottom"),sQuery(id+"F0.wireOp",EDGE,"7a9b5616-fe8a-4a4b-9298-42c4a7e55be2.rect.top"),sQuery(id+"F0.wireOp",EDGE,"208a584b-ce05-4589-bfe7-39b1698a8194.rect.top"),sQuery(id+"F0.wireOp",EDGE,"0ff1be2a-a1a8-4b6e-9f00-62856e441f21.rect.bottom"),sQuery(id+"F0.wireOp",EDGE,"7a9b5616-fe8a-4a4b-9298-42c4a7e55be2.rect.bottom"),sQuery(id+"F0.wireOp",EDGE,"0ff1be2a-a1a8-4b6e-9f00-62856e441f21.rect.top"),sQuery(id+"F0.wireOp",EDGE,"57ca4f26-5c56-4c68-9457-4a64392f3347.rect.top"),sQuery(id+"F0.wireOp",EDGE,"57ca4f26-5c56-4c68-9457-4a64392f3347.rect.bottom"),sQuery(id+"F0.wireOp",EDGE,"04949f4e-e150-414f-b18a-4da78bc3358c.rect.bottom"),sQuery(id+"F0.wireOp",EDGE,"3fd6ee33-8733-46eb-a767-dbbe76983c7d.rect.top"),sQuery(id+"F0.wireOp",EDGE,"3fd6ee33-8733-46eb-a767-dbbe76983c7d.rect.bottom"),sQuery(id+"F0.wireOp",EDGE,"e532b4a8-563d-4d6a-8b1a-a20fa318d2fc.rect.right"),sQuery(id+"F0.wireOp",EDGE,"70cd7b72-5c6a-41ce-aa97-58821a5495a2.rect.left"),sQuery(id+"F0.wireOp",EDGE,"c8e58609-f867-4bb0-9ef6-a67fd09ed313.rect.left"),sQuery(id+"F0.wireOp",EDGE,"7f84faf9-ebf7-483f-8f19-fe061d16c88f.rect.right"),sQuery(id+"F0.wireOp",EDGE,"7939643b-5da5-488a-aeaf-6eee9e5d4f94.rect.left"),sQuery(id+"F0.wireOp",EDGE,"32a260d1-513d-470c-9a95-00da4923ba82.rect.right"),sQuery(id+"F0.wireOp",EDGE,"88e53884-e192-42f0-bd1f-923dc15386a3.rect.right"),sQuery(id+"F0.wireOp",EDGE,"70cd7b72-5c6a-41ce-aa97-58821a5495a2.rect.right"),sQuery(id+"F0.wireOp",EDGE,"e532b4a8-563d-4d6a-8b1a-a20fa318d2fc.rect.left"),sQuery(id+"F0.wireOp",EDGE,"c8e58609-f867-4bb0-9ef6-a67fd09ed313.rect.right"),sQuery(id+"F0.wireOp",EDGE,"7f84faf9-ebf7-483f-8f19-fe061d16c88f.rect.left"),sQuery(id+"F0.wireOp",EDGE,"32a260d1-513d-470c-9a95-00da4923ba82.rect.left"),sQuery(id+"F0.wireOp",EDGE,"f61bf7cc-c32d-46f2-bc22-689eb20f4aa8.rect.right"),sQuery(id+"F0.wireOp",EDGE,"528fd60a-5173-460b-8718-95726cf1d0d3.rect.right"),sQuery(id+"F0.wireOp",EDGE,"7939643b-5da5-488a-aeaf-6eee9e5d4f94.rect.right"),sQuery(id+"F0.wireOp",EDGE,"88e53884-e192-42f0-bd1f-923dc15386a3.rect.left"),sQuery(id+"F0.wireOp",EDGE,"f61bf7cc-c32d-46f2-bc22-689eb20f4aa8.rect.left"),sQuery(id+"F0.wireOp",EDGE,"528fd60a-5173-460b-8718-95726cf1d0d3.rect.left"),sQuery(id+"F0.wireOp",EDGE,"601dbf1e-1562-48c8-971d-08c2e95b1b61.rect.left"),sQuery(id+"F0.wireOp",EDGE,"c8e58609-f867-4bb0-9ef6-a67fd09ed313.rect.bottom"),sQuery(id+"F0.wireOp",EDGE,"88e53884-e192-42f0-bd1f-923dc15386a3.rect.top"),sQuery(id+"F0.wireOp",EDGE,"70cd7b72-5c6a-41ce-aa97-58821a5495a2.rect.bottom"),sQuery(id+"F0.wireOp",EDGE,"75fc349b-8e82-414b-b9d7-0717b741608d.rect.right"),sQuery(id+"F0.wireOp",EDGE,"2ff48f1a-e787-4175-bc96-8065b9f0d86f.rect.top"),sQuery(id+"F0.wireOp",EDGE,"75fc349b-8e82-414b-b9d7-0717b741608d.rect.bottom"),sQuery(id+"F0.wireOp",EDGE,"2ff48f1a-e787-4175-bc96-8065b9f0d86f.rect.left"),sQuery(id+"F0.wireOp",EDGE,"2ff48f1a-e787-4175-bc96-8065b9f0d86f.rect.bottom"),sQuery(id+"F0.wireOp",EDGE,"32a260d1-513d-470c-9a95-00da4923ba82.rect.bottom"),sQuery(id+"F0.wireOp",EDGE,"88e53884-e192-42f0-bd1f-923dc15386a3.rect.bottom"),sQuery(id+"F0.wireOp",EDGE,"528fd60a-5173-460b-8718-95726cf1d0d3.rect.top"),sQuery(id+"F0.wireOp",EDGE,"f61bf7cc-c32d-46f2-bc22-689eb20f4aa8.rect.bottom"),sQuery(id+"F0.wireOp",EDGE,"601dbf1e-1562-48c8-971d-08c2e95b1b61.rect.right"),sQuery(id+"F0.wireOp",EDGE,"7f84faf9-ebf7-483f-8f19-fe061d16c88f.rect.top"),sQuery(id+"F0.wireOp",EDGE,"601dbf1e-1562-48c8-971d-08c2e95b1b61.rect.bottom"),sQuery(id+"F0.wireOp",EDGE,"528fd60a-5173-460b-8718-95726cf1d0d3.rect.bottom"),sQuery(id+"F0.wireOp",EDGE,"e532b4a8-563d-4d6a-8b1a-a20fa318d2fc.rect.top"),sQuery(id+"F0.wireOp",EDGE,"75fc349b-8e82-414b-b9d7-0717b741608d.rect.top"),sQuery(id+"F0.wireOp",EDGE,"601dbf1e-1562-48c8-971d-08c2e95b1b61.rect.top"),sQuery(id+"F0.wireOp",EDGE,"32a260d1-513d-470c-9a95-00da4923ba82.rect.top"),sQuery(id+"F0.wireOp",EDGE,"f61bf7cc-c32d-46f2-bc22-689eb20f4aa8.rect.top"),sQuery(id+"F0.wireOp",EDGE,"7f84faf9-ebf7-483f-8f19-fe061d16c88f.rect.bottom"),sQuery(id+"F0.wireOp",EDGE,"e532b4a8-563d-4d6a-8b1a-a20fa318d2fc.rect.bottom"),sQuery(id+"F0.wireOp",EDGE,"70cd7b72-5c6a-41ce-aa97-58821a5495a2.rect.top"),sQuery(id+"F0.wireOp",EDGE,"75fc349b-8e82-414b-b9d7-0717b741608d.rect.left"),sQuery(id+"F0.wireOp",EDGE,"7939643b-5da5-488a-aeaf-6eee9e5d4f94.rect.bottom"),sQuery(id+"F0.wireOp",EDGE,"7939643b-5da5-488a-aeaf-6eee9e5d4f94.rect.top"),sQuery(id+"F0.wireOp",EDGE,"c8e58609-f867-4bb0-9ef6-a67fd09ed313.rect.top"),sQuery(id+"F0.wireOp",EDGE,"2ff48f1a-e787-4175-bc96-8065b9f0d86f.rect.right"),sQuery(id+"F0.wireOp",EDGE,"34bcf3fd-ed4a-4185-adf8-dc405735c649.rect.left"),sQuery(id+"F0.wireOp",EDGE,"e34a8003-39e3-4020-9972-05b17e0e0dd2.rect.right"),sQuery(id+"F0.wireOp",EDGE,"5d584f02-6df5-43d9-a6c0-44b15491b2ef.rect.right"),sQuery(id+"F0.wireOp",EDGE,"5d584f02-6df5-43d9-a6c0-44b15491b2ef.rect.left"),sQuery(id+"F0.wireOp",EDGE,"34bcf3fd-ed4a-4185-adf8-dc405735c649.rect.right"),sQuery(id+"F0.wireOp",EDGE,"e34a8003-39e3-4020-9972-05b17e0e0dd2.rect.left"),sQuery(id+"F0.wireOp",EDGE,"5d584f02-6df5-43d9-a6c0-44b15491b2ef.rect.bottom"),sQuery(id+"F0.wireOp",EDGE,"e34a8003-39e3-4020-9972-05b17e0e0dd2.rect.top"),sQuery(id+"F0.wireOp",EDGE,"e34a8003-39e3-4020-9972-05b17e0e0dd2.rect.bottom"),sQuery(id+"F0.wireOp",EDGE,"34bcf3fd-ed4a-4185-adf8-dc405735c649.rect.bottom"),sQuery(id+"F0.wireOp",EDGE,"34bcf3fd-ed4a-4185-adf8-dc405735c649.rect.top"),sQuery(id+"F0.wireOp",EDGE,"5d584f02-6df5-43d9-a6c0-44b15491b2ef.rect.top"),sQuery(id+"F0.wireOp",EDGE,"af60b362-f3e8-441e-9e1f-4259201feecf.rect.top"),sQuery(id+"F0.wireOp",EDGE,"E9.rect.bottom"),sQuery(id+"F0.wireOp",EDGE,"4a09bc43-db4a-4a7f-b510-9db42ac8ae9a.rect.top"),sQuery(id+"F0.wireOp",EDGE,"74e83cdb-cc94-4001-ac12-18727aacc957.rect.bottom"),sQuery(id+"F0.wireOp",EDGE,"242bfa70-7804-440d-99c3-28ec5b1ee65b.rect.left"),sQuery(id+"F0.wireOp",EDGE,"52d42c98-a837-46c3-ad31-eb32c8073d4f.rect.bottom"),sQuery(id+"F0.wireOp",EDGE,"af60b362-f3e8-441e-9e1f-4259201feecf.rect.left"),sQuery(id+"F0.wireOp",EDGE,"9a44f7b1-bce2-4215-bd6e-a2994b21c9db.rect.left"),sQuery(id+"F0.wireOp",EDGE,"9a44f7b1-bce2-4215-bd6e-a2994b21c9db.rect.top"),sQuery(id+"F0.wireOp",EDGE,"8898d686-7fb0-4204-8ff5-b49aa4418833.rect.bottom"),sQuery(id+"F0.wireOp",EDGE,"af60b362-f3e8-441e-9e1f-4259201feecf.rect.bottom"),sQuery(id+"F0.wireOp",EDGE,"47ae59bc-59bf-44a3-84ce-727988fe69e2.rect.top"),sQuery(id+"F0.wireOp",EDGE,"bc846ad1-a97c-4f09-9111-d1a515cad6f8.rect.bottom"),sQuery(id+"F0.wireOp",EDGE,"4a09bc43-db4a-4a7f-b510-9db42ac8ae9a.rect.right"),sQuery(id+"F0.wireOp",EDGE,"c0278d55-c928-4a3d-bbfd-8237f96a4b24.rect.top"),sQuery(id+"F0.wireOp",EDGE,"9a44f7b1-bce2-4215-bd6e-a2994b21c9db.rect.right"),sQuery(id+"F0.wireOp",EDGE,"c5aef39c-5632-48cf-8677-54e9030eb2c4.rect.bottom"),sQuery(id+"F0.wireOp",EDGE,"E10.rect.bottom"),sQuery(id+"F0.wireOp",EDGE,"E12.rect.bottom"),sQuery(id+"F0.wireOp",EDGE,"E13.rect.bottom"),sQuery(id+"F0.wireOp",EDGE,"b3a627d4-5a3a-4939-a623-0a0e6fe677c3.rect.top"),sQuery(id+"F0.wireOp",EDGE,"18b0f6b7-df90-4cf5-9876-91a50f2eee23.rect.top"),sQuery(id+"F0.wireOp",EDGE,"63a51c63-2273-4610-9e31-61f28d7edbfb.rect.top"),sQuery(id+"F0.wireOp",EDGE,"53dead6a-162f-43fe-8eb7-e704184291b4.rect.top"),sQuery(id+"F0.wireOp",EDGE,"c747e2a2-d4de-4c95-9238-e19881138373.rect.bottom"),sQuery(id+"F0.wireOp",EDGE,"118694ef-aa59-4623-b280-3f1e087cdfaa.rect.top"),sQuery(id+"F0.wireOp",EDGE,"360e989a-c57f-4c8e-90cd-6aefb2f6df26.rect.bottom"),sQuery(id+"F0.wireOp",EDGE,"9d1cec2a-90ec-449a-97f7-b9412bb1a96b.rect.right"),sQuery(id+"F0.wireOp",EDGE,"4a09bc43-db4a-4a7f-b510-9db42ac8ae9a.rect.left"),sQuery(id+"F0.wireOp",EDGE,"E9.rect.top"),sQuery(id+"F0.wireOp",EDGE,"E9.rect.left"),sQuery(id+"F0.wireOp",EDGE,"E9.rect.right"),sQuery(id+"F0.wireOp",EDGE,"ae8f8616-9d58-4ffb-8a16-d6d7847518c4.rect.top"),sQuery(id+"F0.wireOp",EDGE,"9d1cec2a-90ec-449a-97f7-b9412bb1a96b.rect.bottom"),sQuery(id+"F0.wireOp",EDGE,"E12.rect.left"),sQuery(id+"F0.wireOp",EDGE,"242bfa70-7804-440d-99c3-28ec5b1ee65b.rect.top"),sQuery(id+"F0.wireOp",EDGE,"E12.rect.right"),sQuery(id+"F0.wireOp",EDGE,"242bfa70-7804-440d-99c3-28ec5b1ee65b.rect.bottom"),sQuery(id+"F0.wireOp",EDGE,"E11.rect.top"),sQuery(id+"F0.wireOp",EDGE,"9d1cec2a-90ec-449a-97f7-b9412bb1a96b.rect.left"),sQuery(id+"F0.wireOp",EDGE,"242bfa70-7804-440d-99c3-28ec5b1ee65b.rect.right"),sQuery(id+"F0.wireOp",EDGE,"af60b362-f3e8-441e-9e1f-4259201feecf.rect.right"),sQuery(id+"F0.wireOp",EDGE,"c747e2a2-d4de-4c95-9238-e19881138373.rect.left"),sQuery(id+"F0.wireOp",EDGE,"E10.rect.top"),sQuery(id+"F0.wireOp",EDGE,"53dead6a-162f-43fe-8eb7-e704184291b4.rect.left"),sQuery(id+"F0.wireOp",EDGE,"360e989a-c57f-4c8e-90cd-6aefb2f6df26.rect.top"),sQuery(id+"F0.wireOp",EDGE,"2cb47c05-e519-4d57-b594-34d3ae56e2c8.rect.top"),sQuery(id+"F0.wireOp",EDGE,"118694ef-aa59-4623-b280-3f1e087cdfaa.rect.bottom"),sQuery(id+"F0.wireOp",EDGE,"bc846ad1-a97c-4f09-9111-d1a515cad6f8.rect.right"),sQuery(id+"F0.wireOp",EDGE,"435473e4-aa7a-485e-8a0a-2050a405410e.rect.bottom"),sQuery(id+"F0.wireOp",EDGE,"52d42c98-a837-46c3-ad31-eb32c8073d4f.rect.left"),sQuery(id+"F0.wireOp",EDGE,"63a51c63-2273-4610-9e31-61f28d7edbfb.rect.left"),sQuery(id+"F0.wireOp",EDGE,"4a09bc43-db4a-4a7f-b510-9db42ac8ae9a.rect.bottom"),sQuery(id+"F0.wireOp",EDGE,"ae8f8616-9d58-4ffb-8a16-d6d7847518c4.rect.right"),sQuery(id+"F0.wireOp",EDGE,"53dead6a-162f-43fe-8eb7-e704184291b4.rect.bottom"),sQuery(id+"F0.wireOp",EDGE,"bc846ad1-a97c-4f09-9111-d1a515cad6f8.rect.left"),sQuery(id+"F0.wireOp",EDGE,"74e83cdb-cc94-4001-ac12-18727aacc957.rect.right"),sQuery(id+"F0.wireOp",EDGE,"52d42c98-a837-46c3-ad31-eb32c8073d4f.rect.top"),sQuery(id+"F0.wireOp",EDGE,"435473e4-aa7a-485e-8a0a-2050a405410e.rect.top"),sQuery(id+"F0.wireOp",EDGE,"297ca8d3-144b-4ea2-a4cc-06fbe6e60c2f.rect.bottom"),sQuery(id+"F0.wireOp",EDGE,"118694ef-aa59-4623-b280-3f1e087cdfaa.rect.left"),sQuery(id+"F0.wireOp",EDGE,"c5aef39c-5632-48cf-8677-54e9030eb2c4.rect.top"),sQuery(id+"F0.wireOp",EDGE,"ae8f8616-9d58-4ffb-8a16-d6d7847518c4.rect.bottom"),sQuery(id+"F0.wireOp",EDGE,"bc846ad1-a97c-4f09-9111-d1a515cad6f8.rect.top"),sQuery(id+"F0.wireOp",EDGE,"74e83cdb-cc94-4001-ac12-18727aacc957.rect.left"),sQuery(id+"F0.wireOp",EDGE,"74e83cdb-cc94-4001-ac12-18727aacc957.rect.top"),sQuery(id+"F0.wireOp",EDGE,"297ca8d3-144b-4ea2-a4cc-06fbe6e60c2f.rect.left"),sQuery(id+"F0.wireOp",EDGE,"8898d686-7fb0-4204-8ff5-b49aa4418833.rect.top"),sQuery(id+"F0.wireOp",EDGE,"360e989a-c57f-4c8e-90cd-6aefb2f6df26.rect.left"),sQuery(id+"F0.wireOp",EDGE,"9a44f7b1-bce2-4215-bd6e-a2994b21c9db.rect.bottom"),sQuery(id+"F0.wireOp",EDGE,"47ae59bc-59bf-44a3-84ce-727988fe69e2.rect.bottom"),sQuery(id+"F0.wireOp",EDGE,"b3a627d4-5a3a-4939-a623-0a0e6fe677c3.rect.right"),sQuery(id+"F0.wireOp",EDGE,"435473e4-aa7a-485e-8a0a-2050a405410e.rect.right"),sQuery(id+"F0.wireOp",EDGE,"E10.rect.right"),sQuery(id+"F0.wireOp",EDGE,"47ae59bc-59bf-44a3-84ce-727988fe69e2.rect.left"),sQuery(id+"F0.wireOp",EDGE,"c5aef39c-5632-48cf-8677-54e9030eb2c4.rect.right"),sQuery(id+"F0.wireOp",EDGE,"8898d686-7fb0-4204-8ff5-b49aa4418833.rect.right"),sQuery(id+"F0.wireOp",EDGE,"63a51c63-2273-4610-9e31-61f28d7edbfb.rect.bottom"),sQuery(id+"F0.wireOp",EDGE,"E13.rect.right"),sQuery(id+"F0.wireOp",EDGE,"E13.rect.left"),sQuery(id+"F0.wireOp",EDGE,"E13.rect.top"),sQuery(id+"F0.wireOp",EDGE,"118694ef-aa59-4623-b280-3f1e087cdfaa.rect.right"),sQuery(id+"F0.wireOp",EDGE,"c747e2a2-d4de-4c95-9238-e19881138373.rect.top"),sQuery(id+"F0.wireOp",EDGE,"8898d686-7fb0-4204-8ff5-b49aa4418833.rect.left"),sQuery(id+"F0.wireOp",EDGE,"c5aef39c-5632-48cf-8677-54e9030eb2c4.rect.left"),sQuery(id+"F0.wireOp",EDGE,"297ca8d3-144b-4ea2-a4cc-06fbe6e60c2f.rect.right"),sQuery(id+"F0.wireOp",EDGE,"63a51c63-2273-4610-9e31-61f28d7edbfb.rect.right"),sQuery(id+"F0.wireOp",EDGE,"2cb47c05-e519-4d57-b594-34d3ae56e2c8.rect.right"),sQuery(id+"F0.wireOp",EDGE,"52d42c98-a837-46c3-ad31-eb32c8073d4f.rect.right"),sQuery(id+"F0.wireOp",EDGE,"E10.rect.left"),sQuery(id+"F0.wireOp",EDGE,"b3a627d4-5a3a-4939-a623-0a0e6fe677c3.rect.left"),sQuery(id+"F0.wireOp",EDGE,"435473e4-aa7a-485e-8a0a-2050a405410e.rect.left"),sQuery(id+"F0.wireOp",EDGE,"297ca8d3-144b-4ea2-a4cc-06fbe6e60c2f.rect.top"),sQuery(id+"F0.wireOp",EDGE,"53dead6a-162f-43fe-8eb7-e704184291b4.rect.right"),sQuery(id+"F0.wireOp",EDGE,"2cb47c05-e519-4d57-b594-34d3ae56e2c8.rect.bottom"),sQuery(id+"F0.wireOp",EDGE,"2cb47c05-e519-4d57-b594-34d3ae56e2c8.rect.left"),sQuery(id+"F0.wireOp",EDGE,"ae8f8616-9d58-4ffb-8a16-d6d7847518c4.rect.left"),sQuery(id+"F0.wireOp",EDGE,"360e989a-c57f-4c8e-90cd-6aefb2f6df26.rect.right"),sQuery(id+"F0.wireOp",EDGE,"47ae59bc-59bf-44a3-84ce-727988fe69e2.rect.right"),sQuery(id+"F0.wireOp",EDGE,"b3a627d4-5a3a-4939-a623-0a0e6fe677c3.rect.bottom"),sQuery(id+"F0.wireOp",EDGE,"E14.rect.top"),sQuery(id+"F0.wireOp",EDGE,"c747e2a2-d4de-4c95-9238-e19881138373.rect.right"),sQuery(id+"F0.wireOp",EDGE,"E11.rect.left"),sQuery(id+"F0.wireOp",EDGE,"47dfa867-ac7e-48c2-bdf9-ba484dec7aad.rect.bottom"),sQuery(id+"F0.wireOp",EDGE,"E14.rect.left"),sQuery(id+"F0.wireOp",EDGE,"47dfa867-ac7e-48c2-bdf9-ba484dec7aad.rect.top"),sQuery(id+"F0.wireOp",EDGE,"E14.rect.bottom"),sQuery(id+"F0.wireOp",EDGE,"E11.rect.right"),sQuery(id+"F0.wireOp",EDGE,"E14.rect.right"),sQuery(id+"F0.wireOp",EDGE,"47dfa867-ac7e-48c2-bdf9-ba484dec7aad.rect.right"),sQuery(id+"F0.wireOp",EDGE,"18b0f6b7-df90-4cf5-9876-91a50f2eee23.rect.left"),sQuery(id+"F0.wireOp",EDGE,"E12.rect.top"),sQuery(id+"F0.wireOp",EDGE,"c0278d55-c928-4a3d-bbfd-8237f96a4b24.rect.right"),sQuery(id+"F0.wireOp",EDGE,"c0278d55-c928-4a3d-bbfd-8237f96a4b24.rect.bottom"),sQuery(id+"F0.wireOp",EDGE,"9d1cec2a-90ec-449a-97f7-b9412bb1a96b.rect.top"),sQuery(id+"F0.wireOp",EDGE,"18b0f6b7-df90-4cf5-9876-91a50f2eee23.rect.bottom"),sQuery(id+"F0.wireOp",EDGE,"18b0f6b7-df90-4cf5-9876-91a50f2eee23.rect.right"),sQuery(id+"F0.wireOp",EDGE,"c0278d55-c928-4a3d-bbfd-8237f96a4b24.rect.left"),sQuery(id+"F0.wireOp",EDGE,"47dfa867-ac7e-48c2-bdf9-ba484dec7aad.rect.left"),sQuery(id+"F0.wireOp",EDGE,"E11.rect.bottom"),sQuery(id+"F0.wireOp",EDGE,"E15"),sQuery(id+"F0.wireOp",EDGE,"E16")])],"isStart":true});
            var sketch = newSketch(context, id + "F2", { "sketchPlane" : qUnion([Q0])});
            skLineSegment(sketch, "E185.bottom", {"start": v(-3, 3) * mm, "end": v(46.84, 3) * mm});
            skLineSegment(sketch, "E185.top", {"start": v(-3, -180.44) * mm, "end": v(46.84, -180.44) * mm});
            skLineSegment(sketch, "E185.left", {"start": v(-3, 3) * mm, "end": v(-3, -180.44) * mm});
            skLineSegment(sketch, "E185.right", {"start": v(46.84, 3) * mm, "end": v(46.84, -180.44) * mm});
            skCircle(sketch, "E186", {"center": v(43.84, 0) * mm, "radius": 1.38 * mm});
            skCircle(sketch, "E187", {"center": v(0, -177.44) * mm, "radius": 1.38 * mm});
            skSolve(sketch);
        }
        {
            var Q0;
            Q0=qSketchRegion(id+"F2",true);
            extrude(context, id + "F3", {"entities" : qUnion([Q0]), "operationType" : NewBodyOperationType.ADD, "depth" : 3 * mm});
        }
    });
